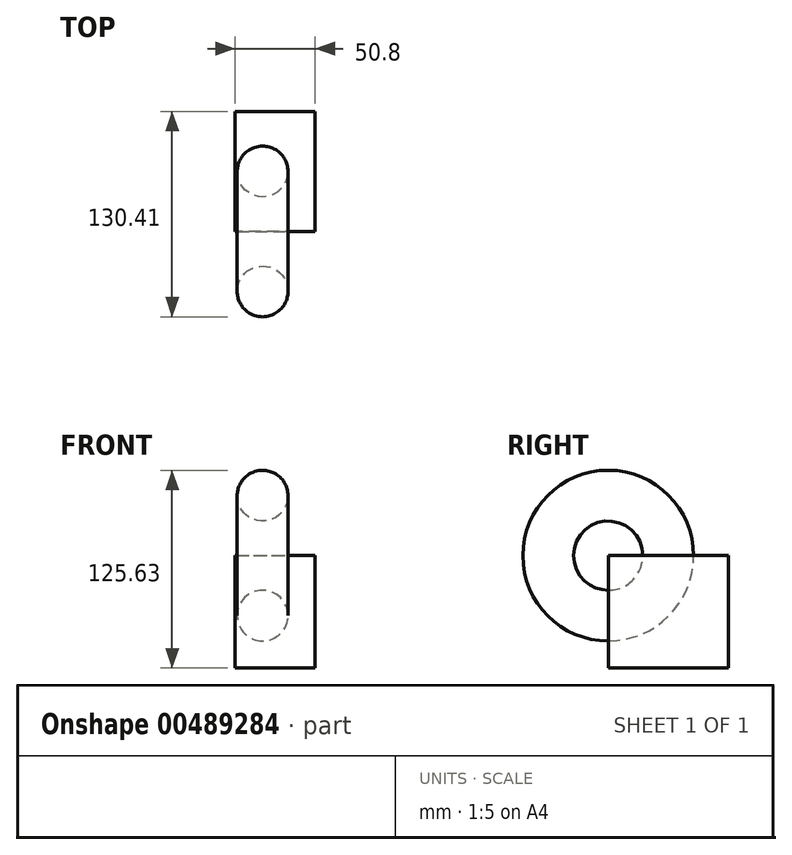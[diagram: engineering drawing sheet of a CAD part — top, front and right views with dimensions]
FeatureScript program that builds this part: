
annotation { "Feature Type Name" : "Feature", "Feature Type Description" : "" }
export const myFeature = defineFeature(function(context is Context, id is Id, definition is map)
    precondition{}
    {
        {
            var Q0;
            Q0=qCreatedBy(makeId("Front.planeOp"),FACE);
            var sketch = newSketch(context, id + "F0", { "sketchPlane" : qUnion([Q0])});
            skLineSegment(sketch, "E0.bottom", {"start": v(38.37, 35.71) * mm, "end": v(-12.43, 35.71) * mm});
            skLineSegment(sketch, "E0.top", {"start": v(38.37, -35.71) * mm, "end": v(-12.43, -35.71) * mm});
            skLineSegment(sketch, "E0.left", {"start": v(38.37, 35.71) * mm, "end": v(38.37, -35.71) * mm});
            skLineSegment(sketch, "E0.right", {"start": v(-12.43, 35.71) * mm, "end": v(-12.43, -35.71) * mm});
            skPoint(sketch, "E0.middle", {"position": v(12.97, 0) * mm});
            skSolve(sketch);
        }
        {
            var Q0;
            Q0 = qSketchRegion(id + "F0", true);
            extrude(context, id + "F1", {"entities" : qUnion([Q0]), "depth" : 76.2 * mm, "hasDraft" : true, "draftAngle" : 0 * degree});
        }
        {
            var Q0;
            Q0=makeQuery(id+"F1.opExtrude","SWEPT_FACE",FACE,{"disambiguationData":[OSD([sQuery(id+"F0.wireOp",EDGE,"E0.bottom")])]});
            var sketch = newSketch(context, id + "F2", { "sketchPlane" : qUnion([Q0])});
            skCircle(sketch, "E1", {"center": v(4.95, -38.1) * mm, "radius": 16.1 * mm});
            skPoint(sketch, "E1.centerSnap0", {"position": v(-12.43, -38.1) * mm});
            skSolve(sketch);
        }
        {
            var Q0;
            Q0=makeQuery(id+"F2.imprint","IMPRINT",FACE,{"disambiguationData":[TD([[makeQuery(id+"F2.imprint","IMPRINT",EDGE,{"derivedFrom":sQuery(id+"F2.wireOp",EDGE,"E1")}),1.0]])]});
            var Q1;
            Q1=makeQuery(id+"F1.opExtrude","CAP_EDGE",EDGE,{"disambiguationData":[OSD([sQuery(id+"F0.wireOp",EDGE,"E0.bottom")])],"isStart":false});
            revolve(context, id + "F3", {"entities" : qUnion([Q0]), "axis" : qUnion([Q1]), "revolveType" : RevolveType.FULL, "oppositeDirection" : true});
        }
    });
